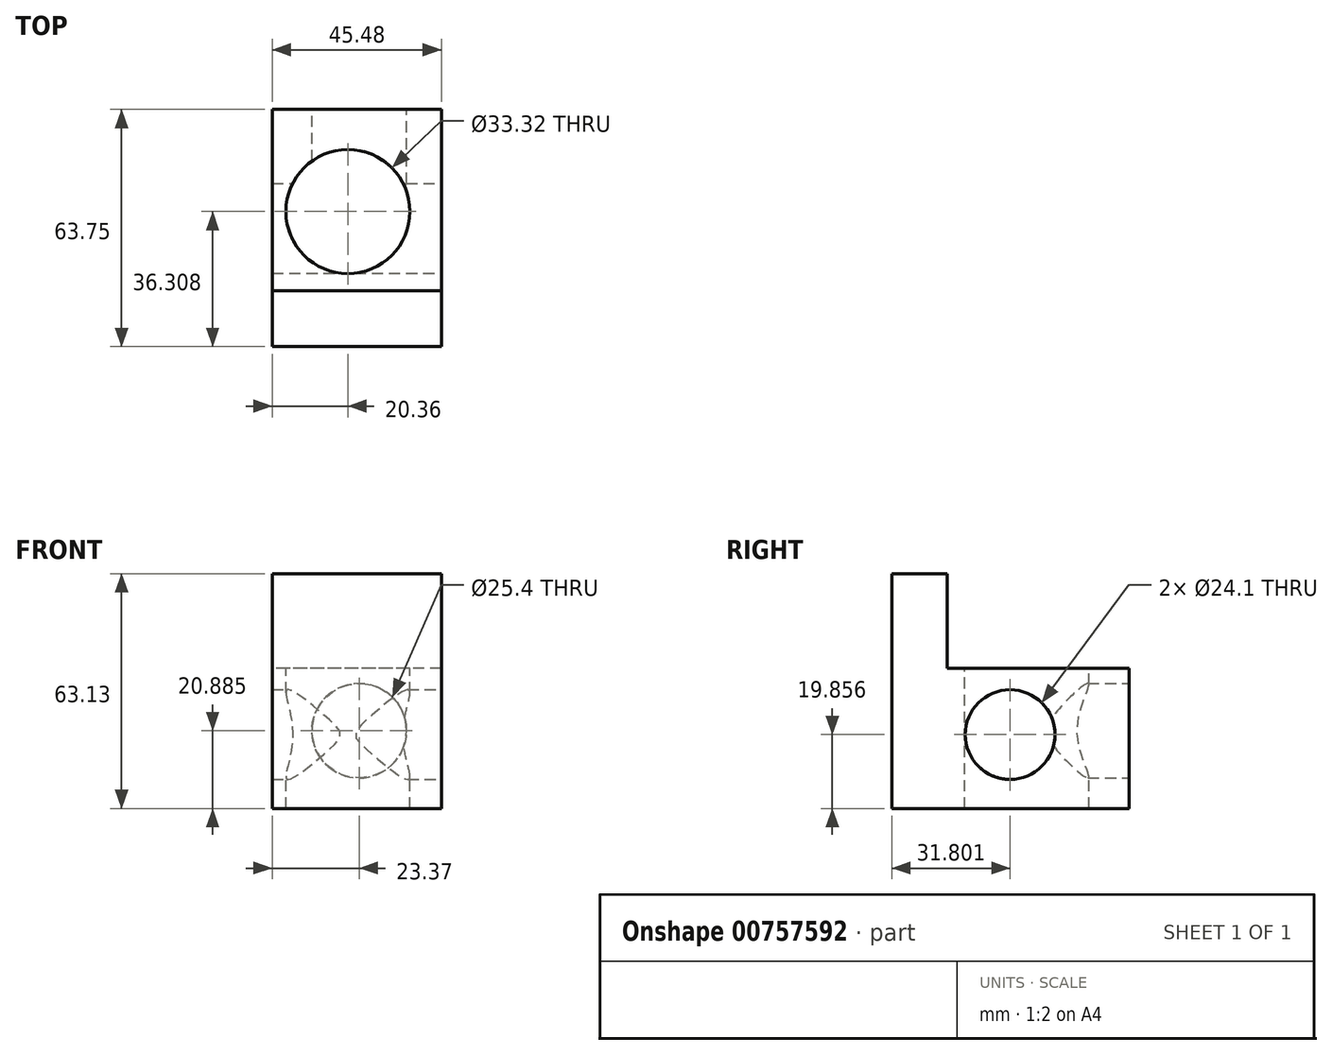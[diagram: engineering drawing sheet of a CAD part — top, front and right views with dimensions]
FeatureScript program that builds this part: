
annotation { "Feature Type Name" : "Feature", "Feature Type Description" : "" }
export const myFeature = defineFeature(function(context is Context, id is Id, definition is map)
    precondition{}
    {
        {
            var Q0;
            Q0=qCreatedBy(makeId("Front.planeOp"),FACE);
            var sketch = newSketch(context, id + "F0", { "sketchPlane" : qUnion([Q0])});
            skLineSegment(sketch, "E0", {"start": v(0, 0) * mm, "end": v(45.48, 0) * mm});
            skLineSegment(sketch, "E1", {"start": v(45.48, 0) * mm, "end": v(45.48, 37.73) * mm});
            skLineSegment(sketch, "E2", {"start": v(45.48, 37.73) * mm, "end": v(0, 37.73) * mm});
            skLineSegment(sketch, "E3", {"start": v(0, 37.73) * mm, "end": v(0, 0) * mm});
            skSolve(sketch);
        }
        {
            var Q0;
            Q0 = qSketchRegion(id + "F0", true);
            extrude(context, id + "F1", {"entities" : qUnion([Q0]), "depth" : 63.75 * mm, "offsetDistance" : 25.4 * mm});
        }
        {
            var Q0;
            Q0=makeQuery(id+"F1.opExtrude","SWEPT_FACE",FACE,{"disambiguationData":[OSD([sQuery(id+"F0.wireOp",EDGE,"E2")])]});
            var sketch = newSketch(context, id + "F2", { "sketchPlane" : qUnion([Q0])});
            skCircle(sketch, "E4", {"center": v(20.36, -27.44) * mm, "radius": 16.66 * mm});
            skSolve(sketch);
        }
        {
            var Q0;
            Q0 = qSketchRegion(id + "F2", true);
            extrude(context, id + "F3", {"entities" : qUnion([Q0]), "operationType" : NewBodyOperationType.REMOVE, "oppositeDirection" : true, "depth" : 75.18 * mm, "offsetDistance" : 25.4 * mm});
        }
        {
            var Q0;
            Q0=makeQuery(id+"F1.opExtrude","SWEPT_FACE",FACE,{"disambiguationData":[OSD([sQuery(id+"F0.wireOp",EDGE,"E2")])]});
            var sketch = newSketch(context, id + "F4", { "sketchPlane" : qUnion([Q0])});
            skLineSegment(sketch, "E5.bottom", {"start": v(45.48, -63.75) * mm, "end": v(0, -63.75) * mm});
            skLineSegment(sketch, "E5.top", {"start": v(45.48, -48.8) * mm, "end": v(0, -48.8) * mm});
            skLineSegment(sketch, "E5.left", {"start": v(45.48, -63.75) * mm, "end": v(45.48, -48.8) * mm});
            skLineSegment(sketch, "E5.right", {"start": v(0, -63.75) * mm, "end": v(0, -48.8) * mm});
            skSolve(sketch);
        }
        {
            var Q0;
            Q0=makeQuery(id+"F4.imprint","IMPRINT",FACE,{"disambiguationData":[TD([[makeQuery(id+"F4.imprint","IMPRINT",EDGE,{"derivedFrom":sQuery(id+"F4.wireOp",EDGE,"E5.bottom")}),-1.0]])]});
            extrude(context, id + "F5", {"entities" : qUnion([Q0]), "operationType" : NewBodyOperationType.ADD, "depth" : 25.4 * mm, "offsetDistance" : 25.4 * mm});
        }
        {
            var Q0;
            Q0=makeQuery(id+"F5.opExtrude","CAP_FACE",FACE,{"disambiguationData":[OSD([sQuery(id+"F4.wireOp",EDGE,"E5.bottom"),sQuery(id+"F4.wireOp",EDGE,"E5.top"),sQuery(id+"F4.wireOp",EDGE,"E5.left"),sQuery(id+"F4.wireOp",EDGE,"E5.right")])],"isStart":false});
            var sketch = newSketch(context, id + "F6", { "sketchPlane" : qUnion([Q0])});
            skLineSegment(sketch, "E6", {"start": v(22.74, -63.75) * mm, "end": v(22.74, -48.8) * mm});
            skSolve(sketch);
        }
        {
            var Q0;
            Q0=sQuery(id+"F6.wireOp",EDGE,"E6");
            extrude(context, id + "F7", {"bodyType" : ToolBodyType.SURFACE, "surfaceEntities" : qUnion([Q0]), "oppositeDirection" : true, "depth" : 77.98 * mm, "offsetDistance" : 25.4 * mm});
        }
        {
            var Q0;
            Q0=makeQuery(id+"F5.boolean.opBoolean","MERGE",FACE,{"derivedFrom":[makeQuery(id+"F1.opExtrude","SWEPT_FACE",FACE,{"disambiguationData":[OSD([sQuery(id+"F0.wireOp",EDGE,"E1")])]}),makeQuery(id+"F5.opExtrude","SWEPT_FACE",FACE,{"disambiguationData":[OSD([sQuery(id+"F4.wireOp",EDGE,"E5.left")])]})]});
            var sketch = newSketch(context, id + "F8", { "sketchPlane" : qUnion([Q0])});
            skCircle(sketch, "E7", {"center": v(-31.95, 19.86) * mm, "radius": 12.05 * mm});
            skSolve(sketch);
        }
        {
            var Q0;
            Q0=makeQuery(id+"F8.imprint","IMPRINT",FACE,{"disambiguationData":[TD([[makeQuery(id+"F8.imprint","IMPRINT",EDGE,{"derivedFrom":sQuery(id+"F8.wireOp",EDGE,"E7")}),1.0]])]});
            var sketch = newSketch(context, id + "F9", { "sketchPlane" : qUnion([Q0])});
            skSolve(sketch);
        }
        {
            var Q0;
            Q0 = qSketchRegion(id + "F9", true);
            var Q1;
            Q1=makeQuery(id+"F8.imprint","IMPRINT",FACE,{"disambiguationData":[TD([[makeQuery(id+"F8.imprint","IMPRINT",EDGE,{"derivedFrom":sQuery(id+"F8.wireOp",EDGE,"E7")}),1.0]])]});
            extrude(context, id + "F10", {"entities" : qUnion([Q0, Q1]), "operationType" : NewBodyOperationType.REMOVE, "oppositeDirection" : true, "depth" : 59.44 * mm, "offsetDistance" : 25.4 * mm});
        }
        {
            var Q0;
            Q0=makeQuery(id+"F1.opExtrude","CAP_FACE",FACE,{"disambiguationData":[OSD([sQuery(id+"F0.wireOp",EDGE,"E0"),sQuery(id+"F0.wireOp",EDGE,"E1"),sQuery(id+"F0.wireOp",EDGE,"E2"),sQuery(id+"F0.wireOp",EDGE,"E3")])],"isStart":true});
            var sketch = newSketch(context, id + "F11", { "sketchPlane" : qUnion([Q0])});
            skCircle(sketch, "E8", {"center": v(-23.37, 20.89) * mm, "radius": 12.7 * mm});
            skSolve(sketch);
        }
        {
            var Q0;
            Q0=makeQuery(id+"F11.imprint","IMPRINT",FACE,{"disambiguationData":[TD([[makeQuery(id+"F11.imprint","IMPRINT",EDGE,{"derivedFrom":sQuery(id+"F11.wireOp",EDGE,"E8")}),1.0]])]});
            extrude(context, id + "F12", {"entities" : qUnion([Q0]), "operationType" : NewBodyOperationType.REMOVE, "oppositeDirection" : true, "depth" : 25.4 * mm, "offsetDistance" : 25.4 * mm});
        }
    });
